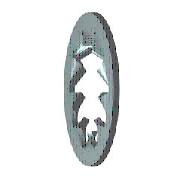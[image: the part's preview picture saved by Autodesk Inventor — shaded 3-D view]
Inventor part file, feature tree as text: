
AUTODESK INVENTOR PART (.ipt)
format: ipt  version: 2015 (Build 190159000, 159)  size: 165,888 bytes
history: native  units: mm (DEFAULTED — no unit token found)
features: sketch x2, extrude x1, pattern_circular x1, plane x1
ambient origin geometry x7: Origin, YZ Plane, XY Plane, X Axis, Y Axis, Z Axis, Center Point
bodies: Solid1 (feature_tree), Body (feature_tree)
feature tree (5):
  extrude  "Cut"  Depth=6.5024mm
  pattern_circular  "Cuts"  [2 undecoded]
  plane  "Work Plane1"
  sketch  "Sketch1"  dims[d0=12.1412mm d1=6.5024mm]
  sketch  "Sketch2"  dims[d2=0.7112mm d3=0.0mm d4=9.3218mm d5=1.963495mm d6=0.7112mm d7=0.0mm d8=0.195072mm d9=80.0mm d11=360.0deg d12=0.0mm d13=0.0mm d18=0.0mm d19=0.0mm]
note: 2 required parameter values undecoded (feature->parameter linkage not recoverable at this tier; creation-order binding heuristic only, values carry confidence <= 0.55)
